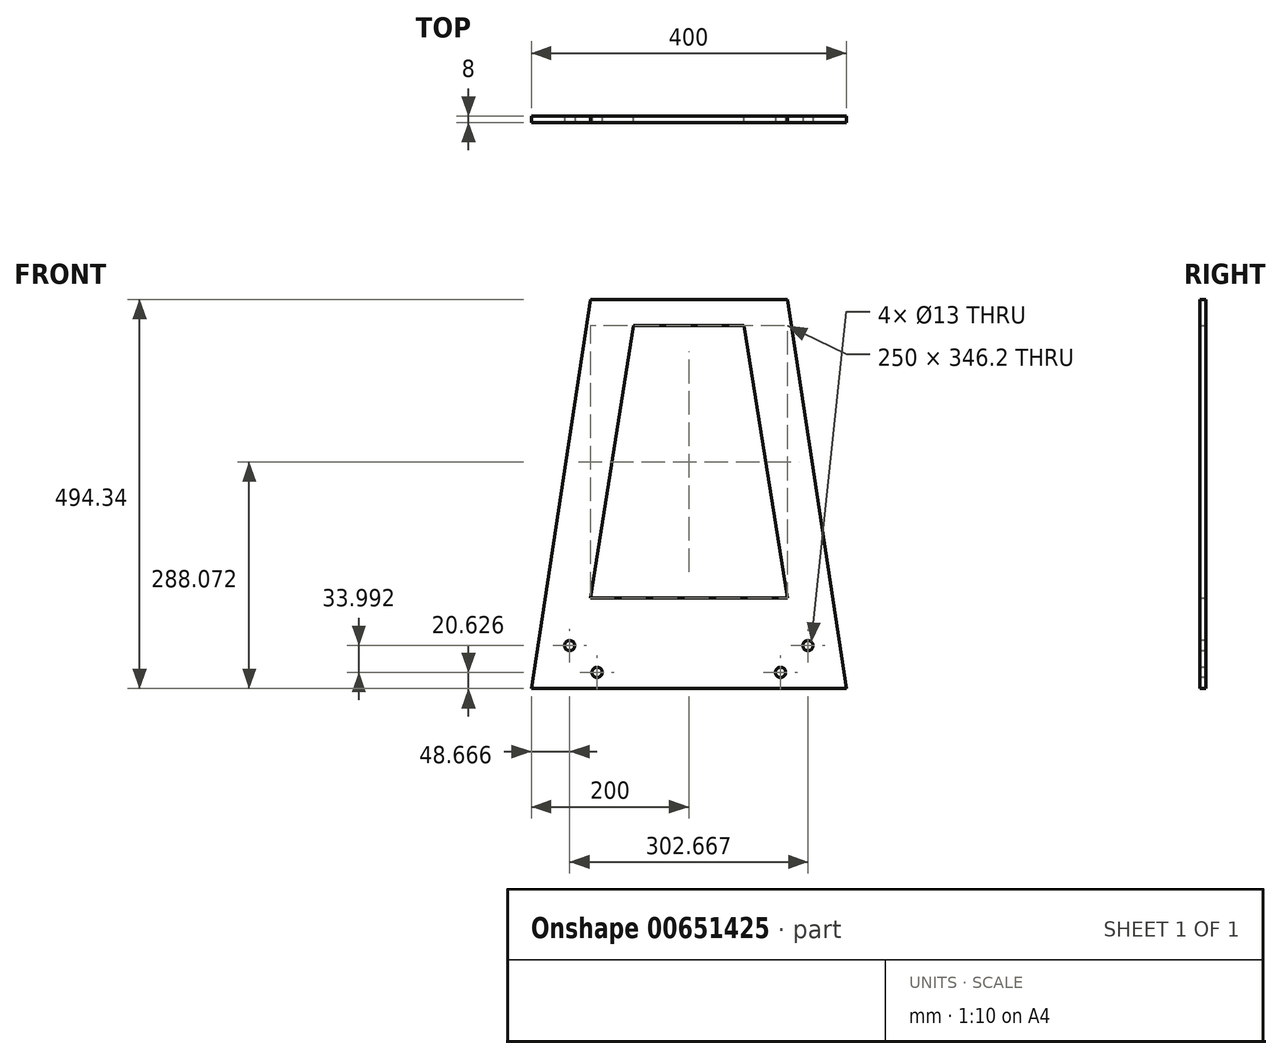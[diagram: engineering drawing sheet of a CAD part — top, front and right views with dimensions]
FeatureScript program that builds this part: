
annotation { "Feature Type Name" : "Feature", "Feature Type Description" : "" }
export const myFeature = defineFeature(function(context is Context, id is Id, definition is map)
    precondition{}
    {
        {
            var Q0;
            Q0=qCreatedBy(makeId("Front.planeOp"),FACE);
            var sketch = newSketch(context, id + "F0", { "sketchPlane" : qUnion([Q0])});
            skLineSegment(sketch, "E0", {"start": v(-200, -247.17) * mm, "end": v(200, -247.17) * mm});
            skLineSegment(sketch, "E1", {"start": v(200, -247.17) * mm, "end": v(125, 247.17) * mm});
            skLineSegment(sketch, "E2", {"start": v(125, 247.17) * mm, "end": v(-125, 247.17) * mm});
            skLineSegment(sketch, "E3", {"start": v(-125, 247.17) * mm, "end": v(-200, -247.17) * mm});
            skLineSegment(sketch, "E4", {"start": v(-70, 214) * mm, "end": v(70, 214) * mm});
            skLineSegment(sketch, "E5", {"start": v(70, 214) * mm, "end": v(125, -132.2) * mm});
            skLineSegment(sketch, "E6", {"start": v(125, -132.2) * mm, "end": v(-125, -132.2) * mm});
            skLineSegment(sketch, "E7", {"start": v(-125, -132.2) * mm, "end": v(-70, 214) * mm});
            skSolve(sketch);
        }
        {
            var Q0;
            Q0 = qSketchRegion(id + "F0", true);
            extrude(context, id + "F1", {"entities" : qUnion([Q0]), "depth" : 8 * mm, "offsetDistance" : 25 * mm});
        }
        {
            var Q0;
            Q0=makeQuery(id+"F1.opExtrude","CAP_FACE",FACE,{"disambiguationData":[OSD([sQuery(id+"F0.wireOp",EDGE,"E0"),sQuery(id+"F0.wireOp",EDGE,"E1"),sQuery(id+"F0.wireOp",EDGE,"E2"),sQuery(id+"F0.wireOp",EDGE,"E3"),sQuery(id+"F0.wireOp",EDGE,"E4"),sQuery(id+"F0.wireOp",EDGE,"E5"),sQuery(id+"F0.wireOp",EDGE,"E6"),sQuery(id+"F0.wireOp",EDGE,"E7")])],"isStart":false});
            var sketch = newSketch(context, id + "F2", { "sketchPlane" : qUnion([Q0])});
            skCircle(sketch, "E8.MirrorC", {"center": v(-116.48, -226.54) * mm, "radius": 6.5 * mm});
            skCircle(sketch, "E9", {"center": v(-151.33, -192.55) * mm, "radius": 6.5 * mm});
            skCircle(sketch, "E10.MirrorC", {"center": v(151.33, -192.55) * mm, "radius": 6.5 * mm});
            skCircle(sketch, "E11.MirrorC", {"center": v(116.48, -226.54) * mm, "radius": 6.5 * mm});
            skSolve(sketch);
        }
        {
            var Q0;
            Q0 = qSketchRegion(id + "F2", true);
            extrude(context, id + "F3", {"entities" : qUnion([Q0]), "operationType" : NewBodyOperationType.REMOVE, "oppositeDirection" : true, "depth" : 25 * mm, "offsetDistance" : 25 * mm});
        }
    });
